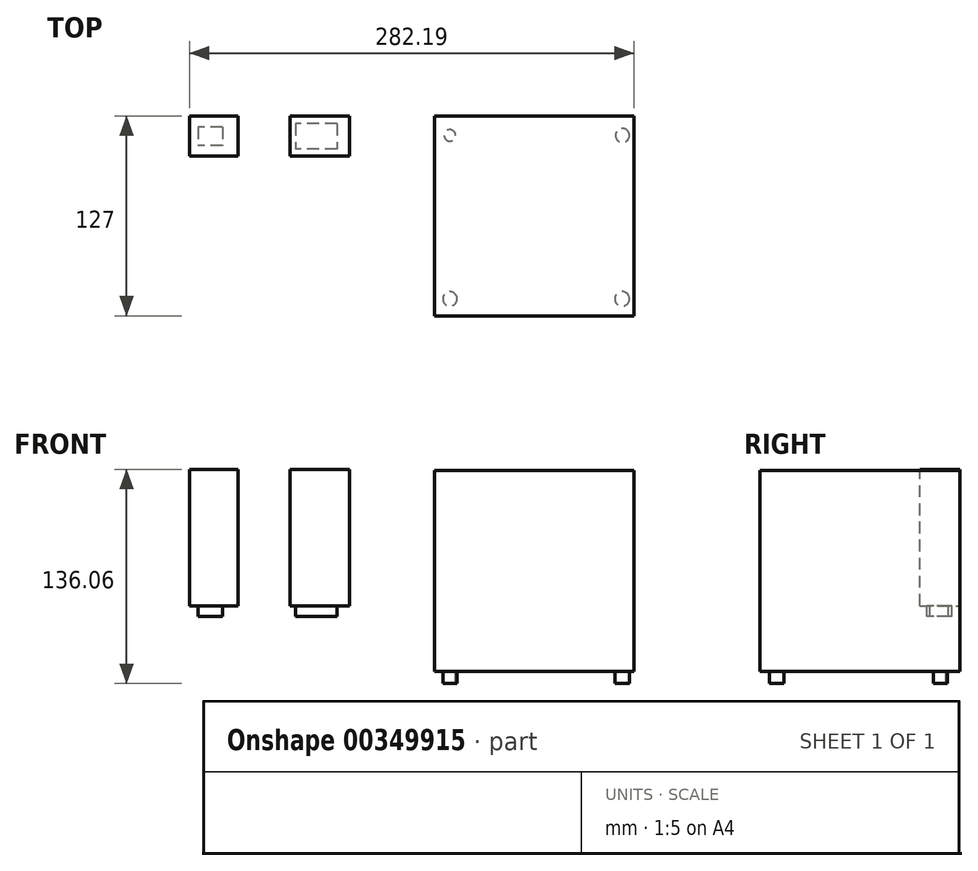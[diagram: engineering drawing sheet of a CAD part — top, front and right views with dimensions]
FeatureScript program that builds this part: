
annotation { "Feature Type Name" : "Feature", "Feature Type Description" : "" }
export const myFeature = defineFeature(function(context is Context, id is Id, definition is map)
    precondition{}
    {
        {
            var Q0;
            Q0=qCreatedBy(makeId("Front.planeOp"),FACE);
            var sketch = newSketch(context, id + "F0", { "sketchPlane" : qUnion([Q0])});
            skLineSegment(sketch, "E0.bottom", {"start": v(63.32, -63.92) * mm, "end": v(-63.32, -63.92) * mm});
            skLineSegment(sketch, "E0.top", {"start": v(63.32, 63.92) * mm, "end": v(-63.32, 63.92) * mm});
            skLineSegment(sketch, "E0.left", {"start": v(63.32, -63.92) * mm, "end": v(63.32, 63.92) * mm});
            skLineSegment(sketch, "E0.right", {"start": v(-63.32, -63.92) * mm, "end": v(-63.32, 63.92) * mm});
            skPoint(sketch, "E0.middle", {"position": v(0, 0) * mm});
            skLineSegment(sketch, "E1.bottom", {"start": v(-117.16, -22.1) * mm, "end": v(-155.06, -22.1) * mm});
            skLineSegment(sketch, "E1.top", {"start": v(-117.16, 64.52) * mm, "end": v(-155.06, 64.52) * mm});
            skLineSegment(sketch, "E1.left", {"start": v(-117.16, -22.1) * mm, "end": v(-117.16, 64.52) * mm});
            skLineSegment(sketch, "E1.right", {"start": v(-155.06, -22.1) * mm, "end": v(-155.06, 64.52) * mm});
            skPoint(sketch, "E1.middle", {"position": v(-136.1, 21.2) * mm});
            skLineSegment(sketch, "E2.bottom", {"start": v(-188.1, -22.1) * mm, "end": v(-218.87, -22.1) * mm});
            skLineSegment(sketch, "E2.top", {"start": v(-188.1, 64.52) * mm, "end": v(-218.87, 64.52) * mm});
            skLineSegment(sketch, "E2.left", {"start": v(-188.1, -22.1) * mm, "end": v(-188.1, 64.52) * mm});
            skLineSegment(sketch, "E2.right", {"start": v(-218.87, -22.1) * mm, "end": v(-218.87, 64.52) * mm});
            skPoint(sketch, "E2.middle", {"position": v(-203.48, 21.2) * mm});
            skSolve(sketch);
        }
        {
            var Q0;
            Q0 = qSketchRegion(id + "F0", true);
            extrude(context, id + "F1", {"entities" : qUnion([Q0]), "depth" : 25.4 * mm, "offsetDistance" : 25.4 * mm});
        }
        {
            var Q0;
            Q0=makeQuery(id+"F1.opExtrude","CAP_FACE",FACE,{"disambiguationData":[OSD([sQuery(id+"F0.wireOp",EDGE,"E0.bottom"),sQuery(id+"F0.wireOp",EDGE,"E0.top"),sQuery(id+"F0.wireOp",EDGE,"E0.left"),sQuery(id+"F0.wireOp",EDGE,"E0.right")])],"isStart":false});
            extrude(context, id + "F2", {"entities" : qUnion([Q0]), "operationType" : NewBodyOperationType.ADD, "depth" : 101.6 * mm, "offsetDistance" : 25.4 * mm});
        }
        {
            var Q0;
            Q0=makeQuery(id+"F1.opExtrude","SWEPT_FACE",FACE,{"disambiguationData":[OSD([sQuery(id+"F0.wireOp",EDGE,"E2.bottom")])]});
            var sketch = newSketch(context, id + "F3", { "sketchPlane" : qUnion([Q0])});
            skLineSegment(sketch, "E3.bottom", {"start": v(-198.01, 7.14) * mm, "end": v(-213.54, 7.14) * mm});
            skLineSegment(sketch, "E3.top", {"start": v(-198.01, 18.92) * mm, "end": v(-213.54, 18.92) * mm});
            skLineSegment(sketch, "E3.left", {"start": v(-198.01, 7.14) * mm, "end": v(-198.01, 18.92) * mm});
            skLineSegment(sketch, "E3.right", {"start": v(-213.54, 7.14) * mm, "end": v(-213.54, 18.92) * mm});
            skPoint(sketch, "E3.middle", {"position": v(-205.77, 13.03) * mm});
            skLineSegment(sketch, "E4.bottom", {"start": v(-125.2, 5) * mm, "end": v(-151.44, 5) * mm});
            skLineSegment(sketch, "E4.top", {"start": v(-125.2, 21.06) * mm, "end": v(-151.44, 21.06) * mm});
            skLineSegment(sketch, "E4.left", {"start": v(-125.2, 5) * mm, "end": v(-125.2, 21.06) * mm});
            skLineSegment(sketch, "E4.right", {"start": v(-151.44, 5) * mm, "end": v(-151.44, 21.06) * mm});
            skPoint(sketch, "E4.middle", {"position": v(-138.32, 13.03) * mm});
            skSolve(sketch);
        }
        {
            var Q0;
            Q0 = qSketchRegion(id + "F3", true);
            extrude(context, id + "F4", {"entities" : qUnion([Q0]), "depth" : 6.86 * mm, "offsetDistance" : 25.4 * mm});
        }
        {
            var Q0;
            {var subQ0=sQuery(id+"F0.wireOp",EDGE,"E0.bottom");Q0=makeQuery(id+"F2.boolean.opBoolean","MERGE",FACE,{"derivedFrom":[makeQuery(id+"F1.opExtrude","SWEPT_FACE",FACE,{"disambiguationData":[OSD([subQ0])]}),makeQuery(id+"F2.opExtrude","SWEPT_FACE",FACE,{"disambiguationData":[OSD([subQ0])]})]});}
            var sketch = newSketch(context, id + "F5", { "sketchPlane" : qUnion([Q0])});
            skCircle(sketch, "E5", {"center": v(-53.53, 116.19) * mm, "radius": 4.54 * mm});
            skCircle(sketch, "E6", {"center": v(55.83, 116.19) * mm, "radius": 4.63 * mm});
            skCircle(sketch, "E7", {"center": v(-53.53, 12.37) * mm, "radius": 3.64 * mm});
            skCircle(sketch, "E8", {"center": v(56.02, 12.37) * mm, "radius": 4.44 * mm});
            skSolve(sketch);
        }
        {
            var Q0;
            Q0 = qSketchRegion(id + "F5", true);
            extrude(context, id + "F6", {"entities" : qUnion([Q0]), "operationType" : NewBodyOperationType.ADD, "depth" : 7.62 * mm, "offsetDistance" : 25.4 * mm});
        }
    });
